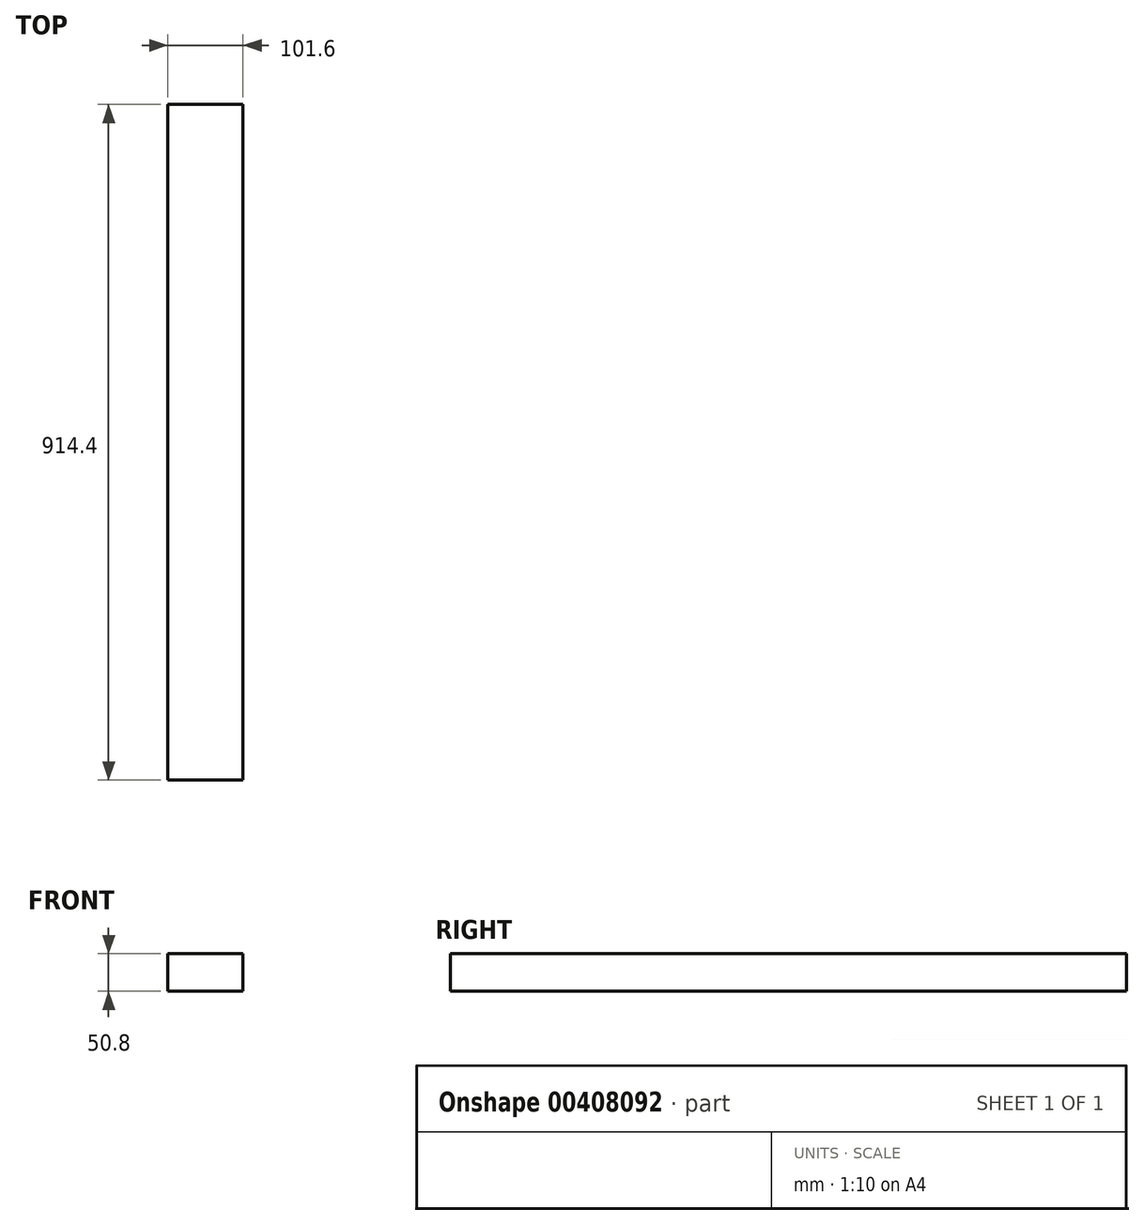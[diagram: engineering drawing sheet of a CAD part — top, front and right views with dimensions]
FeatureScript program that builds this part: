
annotation { "Feature Type Name" : "Feature", "Feature Type Description" : "" }
export const myFeature = defineFeature(function(context is Context, id is Id, definition is map)
    precondition{}
    {
        {
            var Q0;
            Q0=qCreatedBy(makeId("Top.planeOp"),FACE);
            var sketch = newSketch(context, id + "F0", { "sketchPlane" : qUnion([Q0])});
            skLineSegment(sketch, "E0.bottom", {"start": v(50.8, -457.2) * mm, "end": v(-50.8, -457.2) * mm});
            skLineSegment(sketch, "E0.top", {"start": v(50.8, 457.2) * mm, "end": v(-50.8, 457.2) * mm});
            skLineSegment(sketch, "E0.left", {"start": v(50.8, -457.2) * mm, "end": v(50.8, 457.2) * mm});
            skLineSegment(sketch, "E0.right", {"start": v(-50.8, -457.2) * mm, "end": v(-50.8, 457.2) * mm});
            skPoint(sketch, "E0.middle", {"position": v(0, 0) * mm});
            skSolve(sketch);
        }
        {
            var Q0;
            Q0 = qSketchRegion(id + "F0", true);
            extrude(context, id + "F1", {"entities" : qUnion([Q0]), "depth" : 50.8 * mm});
        }
    });
